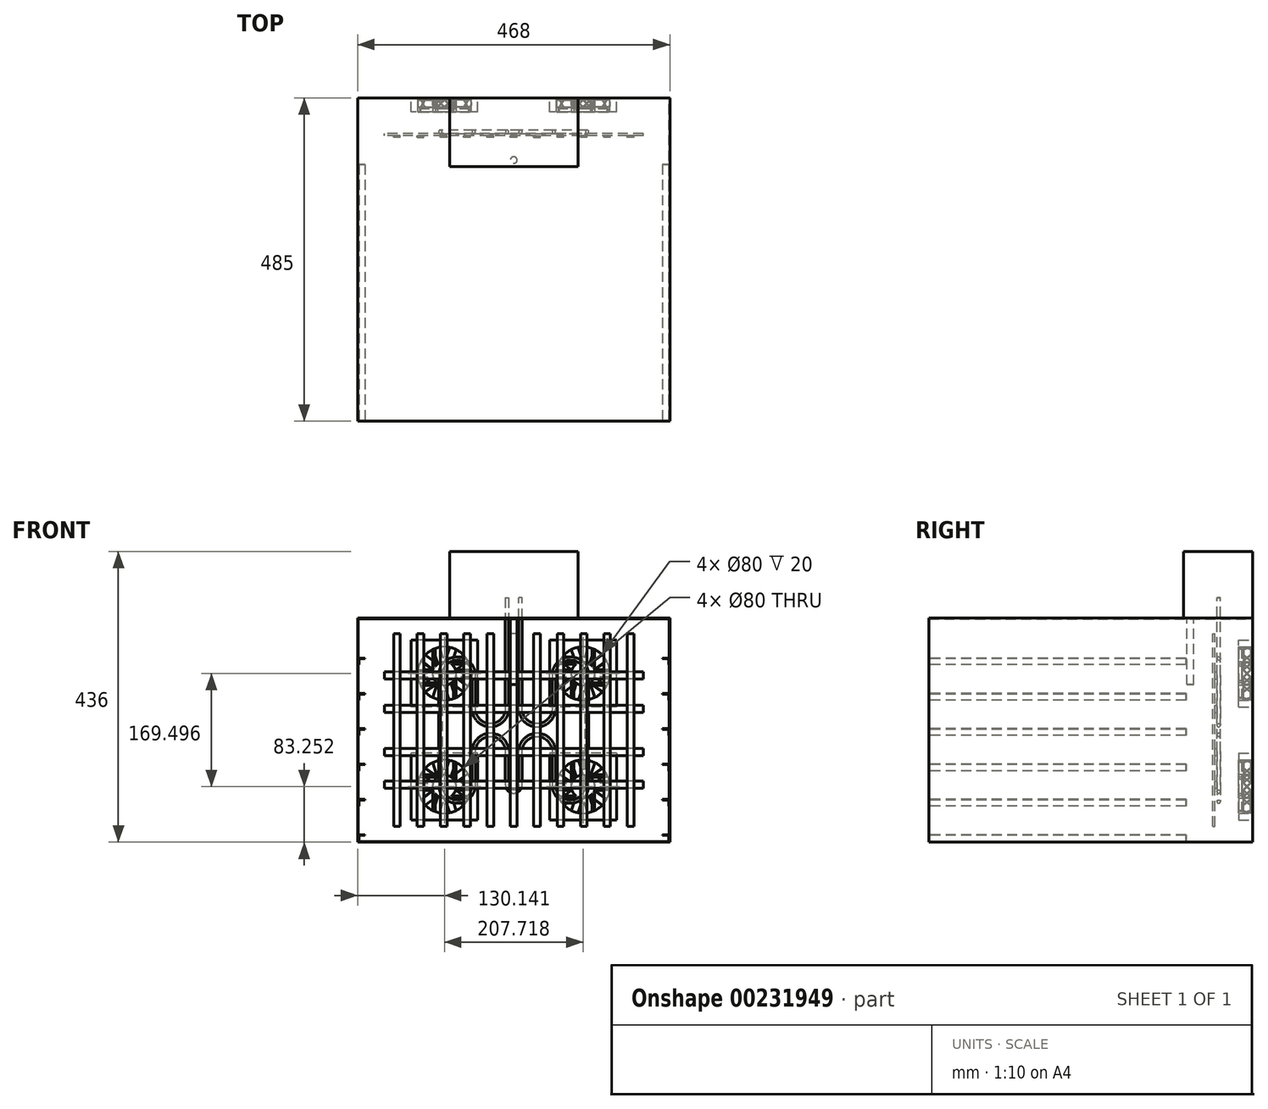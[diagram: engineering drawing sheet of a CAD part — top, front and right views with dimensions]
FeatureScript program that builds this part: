
annotation { "Feature Type Name" : "Feature", "Feature Type Description" : "" }
export const myFeature = defineFeature(function(context is Context, id is Id, definition is map)
    precondition{}
    {
        {
            var Q0;
            Q0=qCreatedBy(makeId("Front.planeOp"),FACE);
            var sketch = newSketch(context, id + "F0", { "sketchPlane" : qUnion([Q0])});
            skLineSegment(sketch, "E0.bottom", {"start": v(234, -168) * mm, "end": v(-234, -168) * mm});
            skLineSegment(sketch, "E0.top", {"start": v(234, 168) * mm, "end": v(-234, 168) * mm});
            skLineSegment(sketch, "E0.left", {"start": v(234, -168) * mm, "end": v(234, 168) * mm});
            skLineSegment(sketch, "E0.right", {"start": v(-234, -168) * mm, "end": v(-234, 168) * mm});
            skPoint(sketch, "E0.middle", {"position": v(0, 0) * mm});
            skSolve(sketch);
        }
        {
            var Q0;
            Q0 = qSketchRegion(id + "F0", true);
            extrude(context, id + "F1", {"entities" : qUnion([Q0]), "depth" : (385 + 50 + 50) * mm});
        }
        {
            var Q0;
            Q0=makeQuery(id+"F1.opExtrude","CAP_FACE",FACE,{"disambiguationData":[OSD([sQuery(id+"F0.wireOp",EDGE,"E0.bottom"),sQuery(id+"F0.wireOp",EDGE,"E0.top"),sQuery(id+"F0.wireOp",EDGE,"E0.left"),sQuery(id+"F0.wireOp",EDGE,"E0.right")])],"isStart":false});
            shell(context, id + "F2", {"entities" : qUnion([Q0]), "thickness" : 1 * mm});
        }
        {
            var Q0;
            Q0=makeQuery(id+"F1.opExtrude","CAP_FACE",FACE,{"disambiguationData":[OSD([sQuery(id+"F0.wireOp",EDGE,"E0.bottom"),sQuery(id+"F0.wireOp",EDGE,"E0.top"),sQuery(id+"F0.wireOp",EDGE,"E0.left"),sQuery(id+"F0.wireOp",EDGE,"E0.right")])],"isStart":false});
            var sketch = newSketch(context, id + "F3", { "sketchPlane" : qUnion([Q0])});
            skLineSegment(sketch, "E1", {"start": v(-233, -167) * mm, "end": v(-233, -157) * mm});
            skLineSegment(sketch, "E2", {"start": v(-233, -157) * mm, "end": v(-223, -157) * mm});
            skLineSegment(sketch, "E3", {"start": v(-223, -157) * mm, "end": v(-223, -158) * mm});
            skLineSegment(sketch, "E4", {"start": v(-223, -158) * mm, "end": v(-232, -158) * mm});
            skLineSegment(sketch, "E5", {"start": v(-232, -158) * mm, "end": v(-232, -167) * mm});
            skLineSegment(sketch, "E6", {"start": v(-232, -167) * mm, "end": v(-233, -167) * mm});
            skLineSegment(sketch, "E7.0.1.0", {"start": v(-232, -105) * mm, "end": v(-232, -114) * mm});
            skLineSegment(sketch, "E7.0.1.1", {"start": v(-223, -105) * mm, "end": v(-232, -105) * mm});
            skLineSegment(sketch, "E7.0.1.2", {"start": v(-233, -104) * mm, "end": v(-223, -104) * mm});
            skLineSegment(sketch, "E7.0.1.3", {"start": v(-233, -114) * mm, "end": v(-233, -104) * mm});
            skLineSegment(sketch, "E7.0.1.4", {"start": v(-232, -114) * mm, "end": v(-233, -114) * mm});
            skLineSegment(sketch, "E7.0.1.5", {"start": v(-223, -104) * mm, "end": v(-223, -105) * mm});
            skLineSegment(sketch, "E7.0.2.0", {"start": v(-232, -52) * mm, "end": v(-232, -61) * mm});
            skLineSegment(sketch, "E7.0.2.1", {"start": v(-223, -52) * mm, "end": v(-232, -52) * mm});
            skLineSegment(sketch, "E7.0.2.2", {"start": v(-233, -51) * mm, "end": v(-223, -51) * mm});
            skLineSegment(sketch, "E7.0.2.3", {"start": v(-233, -61) * mm, "end": v(-233, -51) * mm});
            skLineSegment(sketch, "E7.0.2.4", {"start": v(-232, -61) * mm, "end": v(-233, -61) * mm});
            skLineSegment(sketch, "E7.0.2.5", {"start": v(-223, -51) * mm, "end": v(-223, -52) * mm});
            skLineSegment(sketch, "E7.0.3.0", {"start": v(-232, 1) * mm, "end": v(-232, -8) * mm});
            skLineSegment(sketch, "E7.0.3.1", {"start": v(-223, 1) * mm, "end": v(-232, 1) * mm});
            skLineSegment(sketch, "E7.0.3.2", {"start": v(-233, 2) * mm, "end": v(-223, 2) * mm});
            skLineSegment(sketch, "E7.0.3.3", {"start": v(-233, -8) * mm, "end": v(-233, 2) * mm});
            skLineSegment(sketch, "E7.0.3.4", {"start": v(-232, -8) * mm, "end": v(-233, -8) * mm});
            skLineSegment(sketch, "E7.0.3.5", {"start": v(-223, 2) * mm, "end": v(-223, 1) * mm});
            skLineSegment(sketch, "E7.0.4.0", {"start": v(-232, 54) * mm, "end": v(-232, 45) * mm});
            skLineSegment(sketch, "E7.0.4.1", {"start": v(-223, 54) * mm, "end": v(-232, 54) * mm});
            skLineSegment(sketch, "E7.0.4.2", {"start": v(-233, 55) * mm, "end": v(-223, 55) * mm});
            skLineSegment(sketch, "E7.0.4.3", {"start": v(-233, 45) * mm, "end": v(-233, 55) * mm});
            skLineSegment(sketch, "E7.0.4.4", {"start": v(-232, 45) * mm, "end": v(-233, 45) * mm});
            skLineSegment(sketch, "E7.0.4.5", {"start": v(-223, 55) * mm, "end": v(-223, 54) * mm});
            skLineSegment(sketch, "E7.0.5.0", {"start": v(-232, 107) * mm, "end": v(-232, 98) * mm});
            skLineSegment(sketch, "E7.0.5.1", {"start": v(-223, 107) * mm, "end": v(-232, 107) * mm});
            skLineSegment(sketch, "E7.0.5.2", {"start": v(-233, 108) * mm, "end": v(-223, 108) * mm});
            skLineSegment(sketch, "E7.0.5.3", {"start": v(-233, 98) * mm, "end": v(-233, 108) * mm});
            skLineSegment(sketch, "E7.0.5.4", {"start": v(-232, 98) * mm, "end": v(-233, 98) * mm});
            skLineSegment(sketch, "E7.0.5.5", {"start": v(-223, 108) * mm, "end": v(-223, 107) * mm});
            skLineSegment(sketch, "E7.direction1", {"start": v(-233, -167) * mm, "end": v(-208, -167) * mm, "construction": true});
            skLineSegment(sketch, "E7.direction2", {"start": v(-233, -167) * mm, "end": v(-233, -114) * mm, "construction": true});
            skSolve(sketch);
        }
        {
            var Q0;
            Q0 = qSketchRegion(id + "F3", true);
            var Q1;
            Q1 = qConstructionFilter(qBodyType(qCreatedBy(id + "F3" ,EDGE), BodyType.WIRE), ConstructionObject.NO);
            extrude(context, id + "F4", {"entities" : qUnion([Q0]), "surfaceEntities" : qUnion([Q1]), "oppositeDirection" : true, "depth" : 385 * mm});
        }
        {
            var Q0;
            Q0=makeQuery(id+"F4.opExtrude","SWEPT_BODY",BODY,{"disambiguationData":[OSD([sQuery(id+"F3.wireOp",EDGE,"E7.0.5.0"),sQuery(id+"F3.wireOp",EDGE,"E7.0.5.1"),sQuery(id+"F3.wireOp",EDGE,"E7.0.5.2"),sQuery(id+"F3.wireOp",EDGE,"E7.0.5.3"),sQuery(id+"F3.wireOp",EDGE,"E7.0.5.4"),sQuery(id+"F3.wireOp",EDGE,"E7.0.5.5")])]});
            var Q1;
            Q1=makeQuery(id+"F4.opExtrude","SWEPT_BODY",BODY,{"disambiguationData":[OSD([sQuery(id+"F3.wireOp",EDGE,"E7.0.4.0"),sQuery(id+"F3.wireOp",EDGE,"E7.0.4.1"),sQuery(id+"F3.wireOp",EDGE,"E7.0.4.2"),sQuery(id+"F3.wireOp",EDGE,"E7.0.4.3"),sQuery(id+"F3.wireOp",EDGE,"E7.0.4.4"),sQuery(id+"F3.wireOp",EDGE,"E7.0.4.5")])]});
            var Q2;
            Q2=makeQuery(id+"F4.opExtrude","SWEPT_BODY",BODY,{"disambiguationData":[OSD([sQuery(id+"F3.wireOp",EDGE,"E7.0.3.0"),sQuery(id+"F3.wireOp",EDGE,"E7.0.3.1"),sQuery(id+"F3.wireOp",EDGE,"E7.0.3.2"),sQuery(id+"F3.wireOp",EDGE,"E7.0.3.3"),sQuery(id+"F3.wireOp",EDGE,"E7.0.3.4"),sQuery(id+"F3.wireOp",EDGE,"E7.0.3.5")])]});
            var Q3;
            Q3=makeQuery(id+"F4.opExtrude","SWEPT_BODY",BODY,{"disambiguationData":[OSD([sQuery(id+"F3.wireOp",EDGE,"E7.0.2.0"),sQuery(id+"F3.wireOp",EDGE,"E7.0.2.1"),sQuery(id+"F3.wireOp",EDGE,"E7.0.2.2"),sQuery(id+"F3.wireOp",EDGE,"E7.0.2.3"),sQuery(id+"F3.wireOp",EDGE,"E7.0.2.4"),sQuery(id+"F3.wireOp",EDGE,"E7.0.2.5")])]});
            var Q4;
            Q4=makeQuery(id+"F4.opExtrude","SWEPT_BODY",BODY,{"disambiguationData":[OSD([sQuery(id+"F3.wireOp",EDGE,"E7.0.1.0"),sQuery(id+"F3.wireOp",EDGE,"E7.0.1.1"),sQuery(id+"F3.wireOp",EDGE,"E7.0.1.2"),sQuery(id+"F3.wireOp",EDGE,"E7.0.1.3"),sQuery(id+"F3.wireOp",EDGE,"E7.0.1.4"),sQuery(id+"F3.wireOp",EDGE,"E7.0.1.5")])]});
            var Q5;
            Q5=makeQuery(id+"F4.opExtrude","SWEPT_BODY",BODY,{"disambiguationData":[OSD([sQuery(id+"F3.wireOp",EDGE,"E1"),sQuery(id+"F3.wireOp",EDGE,"E2"),sQuery(id+"F3.wireOp",EDGE,"E3"),sQuery(id+"F3.wireOp",EDGE,"E4"),sQuery(id+"F3.wireOp",EDGE,"E5"),sQuery(id+"F3.wireOp",EDGE,"E6")])]});
            var Q6;
            Q6=qCreatedBy(makeId("Right.planeOp"),FACE);
            mirror(context, id + "F5", {"entities" : qUnion([Q0, Q1, Q2, Q3, Q4, Q5]), "mirrorPlane" : qUnion([Q6])});
        }
        {
            var Q0;
            Q0=makeQuery(id+"F1.opExtrude","CAP_FACE",FACE,{"disambiguationData":[OSD([sQuery(id+"F0.wireOp",EDGE,"E0.bottom"),sQuery(id+"F0.wireOp",EDGE,"E0.top"),sQuery(id+"F0.wireOp",EDGE,"E0.left"),sQuery(id+"F0.wireOp",EDGE,"E0.right")])],"isStart":true});
            var sketch = newSketch(context, id + "F6", { "sketchPlane" : qUnion([Q0])});
            skCircle(sketch, "E8", {"center": v(-103.86, 84.75) * mm, "radius": 40 * mm});
            skCircle(sketch, "E9", {"center": v(103.86, 84.75) * mm, "radius": 40 * mm});
            skCircle(sketch, "E10", {"center": v(103.86, -84.75) * mm, "radius": 40 * mm});
            skCircle(sketch, "E11", {"center": v(-103.86, -84.75) * mm, "radius": 40 * mm});
            skLineSegment(sketch, "E12", {"start": v(0, 0) * mm, "end": v(0, 0) * mm});
            skPoint(sketch, "E12.endSnap0", {"position": v(0, -168) * mm});
            skLineSegment(sketch, "E13", {"start": v(0, 0) * mm, "end": v(275.26, 0) * mm, "construction": true});
            skLineSegment(sketch, "E14", {"start": v(-103.86, 84.75) * mm, "end": v(103.86, 84.75) * mm, "construction": true});
            skLineSegment(sketch, "E15", {"start": v(103.86, 84.75) * mm, "end": v(103.86, -84.75) * mm, "construction": true});
            skLineSegment(sketch, "E16", {"start": v(-103.86, -84.75) * mm, "end": v(-103.86, 84.75) * mm, "construction": true});
            skLineSegment(sketch, "E17", {"start": v(103.86, -84.75) * mm, "end": v(-103.86, -84.75) * mm, "construction": true});
            skSolve(sketch);
        }
        {
            var Q0;
            Q0 = qSketchRegion(id + "F6", true);
            extrude(context, id + "F7", {"entities" : qUnion([Q0]), "operationType" : NewBodyOperationType.REMOVE, "endBound" : BoundingType.THROUGH_ALL, "oppositeDirection" : true, "depth" : 25 * mm});
        }
        {
            var Q0;
            Q0=makeQuery(id+"F2.opShell","OFFSET_FACE",FACE,{"disambiguationData":[OSD([sQuery(id+"F0.wireOp",EDGE,"E0.bottom"),sQuery(id+"F0.wireOp",EDGE,"E0.top"),sQuery(id+"F0.wireOp",EDGE,"E0.left"),sQuery(id+"F0.wireOp",EDGE,"E0.right")])]});
            var sketch = newSketch(context, id + "F8", { "sketchPlane" : qUnion([Q0])});
            skCircle(sketch, "E18.0", {"center": v(-103.86, 84.75) * mm, "radius": 40 * mm});
            skCircle(sketch, "E19.0", {"center": v(103.86, 84.75) * mm, "radius": 40 * mm});
            skCircle(sketch, "E20.0", {"center": v(103.86, -84.75) * mm, "radius": 40 * mm});
            skCircle(sketch, "E21.0", {"center": v(-103.86, -84.75) * mm, "radius": 40 * mm});
            skLineSegment(sketch, "E22.bottom", {"start": v(-53.86, 34.75) * mm, "end": v(-153.86, 34.75) * mm});
            skLineSegment(sketch, "E22.top", {"start": v(-53.86, 134.75) * mm, "end": v(-153.86, 134.75) * mm});
            skLineSegment(sketch, "E22.left", {"start": v(-53.86, 34.75) * mm, "end": v(-53.86, 134.75) * mm});
            skLineSegment(sketch, "E22.right", {"start": v(-153.86, 34.75) * mm, "end": v(-153.86, 134.75) * mm});
            skLineSegment(sketch, "E23.bottom", {"start": v(153.86, 34.75) * mm, "end": v(53.86, 34.75) * mm});
            skLineSegment(sketch, "E23.top", {"start": v(153.86, 134.75) * mm, "end": v(53.86, 134.75) * mm});
            skLineSegment(sketch, "E23.left", {"start": v(153.86, 34.75) * mm, "end": v(153.86, 134.75) * mm});
            skLineSegment(sketch, "E23.right", {"start": v(53.86, 34.75) * mm, "end": v(53.86, 134.75) * mm});
            skLineSegment(sketch, "E24.bottom", {"start": v(153.86, -34.75) * mm, "end": v(53.86, -34.75) * mm});
            skLineSegment(sketch, "E24.top", {"start": v(153.86, -134.75) * mm, "end": v(53.86, -134.75) * mm});
            skLineSegment(sketch, "E24.left", {"start": v(153.86, -34.75) * mm, "end": v(153.86, -134.75) * mm});
            skLineSegment(sketch, "E24.right", {"start": v(53.86, -34.75) * mm, "end": v(53.86, -134.75) * mm});
            skLineSegment(sketch, "E25.bottom", {"start": v(-53.86, -134.75) * mm, "end": v(-153.86, -134.75) * mm});
            skLineSegment(sketch, "E25.top", {"start": v(-53.86, -34.75) * mm, "end": v(-153.86, -34.75) * mm});
            skLineSegment(sketch, "E25.left", {"start": v(-53.86, -134.75) * mm, "end": v(-53.86, -34.75) * mm});
            skLineSegment(sketch, "E25.right", {"start": v(-153.86, -134.75) * mm, "end": v(-153.86, -34.75) * mm});
            skSolve(sketch);
        }
        {
            var Q0;
            Q0 = qSketchRegion(id + "F8", true);
            extrude(context, id + "F9", {"entities" : qUnion([Q0]), "depth" : 20 * mm});
        }
        {
            var Q0;
            Q0=makeQuery(id+"F2.opShell","OFFSET_FACE",FACE,{"disambiguationData":[OSD([sQuery(id+"F0.wireOp",EDGE,"E0.bottom"),sQuery(id+"F0.wireOp",EDGE,"E0.top"),sQuery(id+"F0.wireOp",EDGE,"E0.left"),sQuery(id+"F0.wireOp",EDGE,"E0.right")])]});
            cPlane(context, id + "F10", {"entities" : qUnion([Q0]), "cplaneType" : CPlaneType.OFFSET, "offset" : 50 * mm, "width" : 150 * mm, "height" : 150 * mm});
        }
        {
            var Q0;
            Q0=qCreatedBy(id+"F10.planeOp",FACE);
            var sketch = newSketch(context, id + "F11", { "sketchPlane" : qUnion([Q0])});
            skLineSegment(sketch, "E26", {"start": v(-10, 198.33) * mm, "end": v(-10, 32.24) * mm});
            skLineSegment(sketch, "E27", {"start": v(10, 198.33) * mm, "end": v(10, 32.24) * mm});
            skLineSegment(sketch, "E28", {"start": v(-60, 32.24) * mm, "end": v(-60, 82.24) * mm});
            skLineSegment(sketch, "E29", {"start": v(-110, 82.24) * mm, "end": v(-110, -82.24) * mm});
            skLineSegment(sketch, "E30", {"start": v(-60, -82.24) * mm, "end": v(-60, -32.24) * mm});
            skLineSegment(sketch, "E31", {"start": v(-10, -32.24) * mm, "end": v(-10, -82.24) * mm});
            skLineSegment(sketch, "E32", {"start": v(10, -82.24) * mm, "end": v(10, -32.24) * mm});
            skLineSegment(sketch, "E33", {"start": v(60, -32.24) * mm, "end": v(60, -82.24) * mm});
            skLineSegment(sketch, "E34", {"start": v(110, -82.24) * mm, "end": v(110, 82.24) * mm});
            skLineSegment(sketch, "E35", {"start": v(60, 82.24) * mm, "end": v(60, 32.24) * mm});
            skLineSegment(sketch, "E36", {"start": v(0, 0) * mm, "end": v(0, 56.52) * mm, "construction": true});
            skArc(sketch, "E37", {"start": v(-60, 32.24) * mm, "mid": v(-35, 7.24) * mm, "end": v(-10, 32.24) * mm});
            skArc(sketch, "E38", {"start": v(-60, 82.24) * mm, "mid": v(-85, 107.24) * mm, "end": v(-110, 82.24) * mm});
            skArc(sketch, "E39", {"start": v(10, 32.24) * mm, "mid": v(35, 7.24) * mm, "end": v(60, 32.24) * mm});
            skArc(sketch, "E40", {"start": v(110, 82.24) * mm, "mid": v(85, 107.24) * mm, "end": v(60, 82.24) * mm});
            skArc(sketch, "E41", {"start": v(60, -82.24) * mm, "mid": v(85, -107.24) * mm, "end": v(110, -82.24) * mm});
            skArc(sketch, "E42", {"start": v(60, -32.24) * mm, "mid": v(35, -7.24) * mm, "end": v(10, -32.24) * mm});
            skArc(sketch, "E43", {"start": v(-10, -82.24) * mm, "mid": v(0, -92.24) * mm, "end": v(10, -82.24) * mm});
            skArc(sketch, "E44", {"start": v(-10, -32.24) * mm, "mid": v(-35, -7.24) * mm, "end": v(-60, -32.24) * mm});
            skArc(sketch, "E45", {"start": v(-110, -82.24) * mm, "mid": v(-85, -107.24) * mm, "end": v(-60, -82.24) * mm});
            skLineSegment(sketch, "E46", {"start": v(-60, -32.24) * mm, "end": v(60, -32.24) * mm, "construction": true});
            skLineSegment(sketch, "E47", {"start": v(-60, 32.24) * mm, "end": v(60, 32.24) * mm, "construction": true});
            skLineSegment(sketch, "E48", {"start": v(0, 0) * mm, "end": v(72.76, 0) * mm, "construction": true});
            skSolve(sketch);
        }
        {
            var Q0;
            Q0=sQuery(id+"F11.wireOp",EDGE,"E26");
            var Q1;
            Q1=sQuery(id+"F11.wireOp",VERTEX,"E26.start");
            cPlane(context, id + "F12", {"entities" : qUnion([Q0, Q1]), "cplaneType" : CPlaneType.LINE_POINT, "offset" : 25 * mm, "width" : 150 * mm, "height" : 150 * mm});
        }
        {
            var Q0;
            Q0=qCreatedBy(id+"F12.planeOp",FACE);
            var sketch = newSketch(context, id + "F13", { "sketchPlane" : qUnion([Q0])});
            skCircle(sketch, "E49", {"center": v(-10, 51) * mm, "radius": 2.5 * mm});
            skSolve(sketch);
        }
        {
            var Q0;
            Q0=makeQuery(id+"F13.imprint","IMPRINT",FACE,{"disambiguationData":[TD([[makeQuery(id+"F13.imprint","IMPRINT",EDGE,{"derivedFrom":sQuery(id+"F13.wireOp",EDGE,"E49")}),1.0]])]});
            var Q1;
            Q1 = qConstructionFilter(qBodyType(qCreatedBy(id + "F11" ,EDGE), BodyType.WIRE), ConstructionObject.NO);
            sweep(context, id + "F14", {"profiles" : qUnion([Q0]), "path" : qUnion([Q1])});
        }
        {
            var Q0;
            Q0=qCreatedBy(id+"F10.planeOp",FACE);
            cPlane(context, id + "F15", {"entities" : qUnion([Q0]), "cplaneType" : CPlaneType.OFFSET, "offset" : 2.5 * mm, "width" : 150 * mm, "height" : 150 * mm});
        }
        {
            var Q0;
            Q0=qCreatedBy(id+"F15.planeOp",FACE);
            var sketch = newSketch(context, id + "F16", { "sketchPlane" : qUnion([Q0])});
            skLineSegment(sketch, "E50.bottom", {"start": v(193.88, 26.5) * mm, "end": v(-193.88, 26.5) * mm});
            skLineSegment(sketch, "E50.top", {"start": v(193.88, 37.1) * mm, "end": v(-193.88, 37.1) * mm});
            skLineSegment(sketch, "E50.left", {"start": v(193.88, 26.5) * mm, "end": v(193.88, 37.1) * mm});
            skLineSegment(sketch, "E50.right", {"start": v(-193.88, 26.5) * mm, "end": v(-193.88, 37.1) * mm});
            skPoint(sketch, "E50.middle", {"position": v(0, 31.8) * mm});
            skLineSegment(sketch, "E51.bottom", {"start": v(193.88, 76.52) * mm, "end": v(-193.88, 76.52) * mm});
            skLineSegment(sketch, "E51.top", {"start": v(193.88, 87.12) * mm, "end": v(-193.88, 87.12) * mm});
            skLineSegment(sketch, "E51.left", {"start": v(193.88, 76.52) * mm, "end": v(193.88, 87.12) * mm});
            skLineSegment(sketch, "E51.right", {"start": v(-193.88, 76.52) * mm, "end": v(-193.88, 87.12) * mm});
            skPoint(sketch, "E51.middle", {"position": v(0, 81.82) * mm});
            skLineSegment(sketch, "E52.bottom", {"start": v(193.88, -38.07) * mm, "end": v(-193.88, -38.07) * mm});
            skLineSegment(sketch, "E52.top", {"start": v(193.88, -27.47) * mm, "end": v(-193.88, -27.47) * mm});
            skLineSegment(sketch, "E52.left", {"start": v(193.88, -38.07) * mm, "end": v(193.88, -27.47) * mm});
            skLineSegment(sketch, "E52.right", {"start": v(-193.88, -38.07) * mm, "end": v(-193.88, -27.47) * mm});
            skPoint(sketch, "E52.middle", {"position": v(0, -32.77) * mm});
            skLineSegment(sketch, "E53.bottom", {"start": v(193.88, -87.18) * mm, "end": v(-193.88, -87.18) * mm});
            skLineSegment(sketch, "E53.top", {"start": v(193.88, -76.58) * mm, "end": v(-193.88, -76.58) * mm});
            skLineSegment(sketch, "E53.left", {"start": v(193.88, -87.18) * mm, "end": v(193.88, -76.58) * mm});
            skLineSegment(sketch, "E53.right", {"start": v(-193.88, -87.18) * mm, "end": v(-193.88, -76.58) * mm});
            skPoint(sketch, "E53.middle", {"position": v(0, -81.88) * mm});
            skSolve(sketch);
        }
        {
            var Q0;
            Q0 = qSketchRegion(id + "F16", true);
            extrude(context, id + "F17", {"entities" : qUnion([Q0]), "operationType" : NewBodyOperationType.ADD, "depth" : 3 * mm});
        }
        {
            var Q0;
            Q0=makeQuery(id+"F1.opExtrude","SWEPT_FACE",FACE,{"disambiguationData":[OSD([sQuery(id+"F0.wireOp",EDGE,"E0.top")])]});
            var sketch = newSketch(context, id + "F18", { "sketchPlane" : qUnion([Q0])});
            skLineSegment(sketch, "E54.bottom", {"start": v(96.2, 0) * mm, "end": v(-96.2, 0) * mm});
            skLineSegment(sketch, "E54.top", {"start": v(96.2, -103.28) * mm, "end": v(-96.2, -103.28) * mm});
            skLineSegment(sketch, "E54.left", {"start": v(96.2, 0) * mm, "end": v(96.2, -103.28) * mm});
            skLineSegment(sketch, "E54.right", {"start": v(-96.2, 0) * mm, "end": v(-96.2, -103.28) * mm});
            skPoint(sketch, "E54.middle", {"position": v(0, -51.64) * mm});
            skSolve(sketch);
        }
        {
            var Q0;
            Q0 = qSketchRegion(id + "F18", true);
            extrude(context, id + "F19", {"entities" : qUnion([Q0]), "depth" : 100 * mm});
        }
        {
            var Q0;
            Q0=makeQuery(id+"F1.opExtrude","SWEPT_FACE",FACE,{"disambiguationData":[OSD([sQuery(id+"F0.wireOp",EDGE,"E0.top")])]});
            var sketch = newSketch(context, id + "F20", { "sketchPlane" : qUnion([Q0])});
            skCircle(sketch, "E55", {"center": v(0, -93.28) * mm, "radius": 5 * mm});
            skSolve(sketch);
        }
        {
            var Q0;
            Q0 = qSketchRegion(id + "F20", true);
            extrude(context, id + "F21", {"entities" : qUnion([Q0]), "oppositeDirection" : true, "depth" : 100 * mm});
        }
        {
            var Q0;
            Q0=makeQuery(id+"F9.opExtrude","CAP_FACE",FACE,{"disambiguationData":[OSD([sQuery(id+"F8.wireOp",EDGE,"E18.0"),sQuery(id+"F8.wireOp",EDGE,"E22.bottom"),sQuery(id+"F8.wireOp",EDGE,"E22.top"),sQuery(id+"F8.wireOp",EDGE,"E22.left"),sQuery(id+"F8.wireOp",EDGE,"E22.right")])],"isStart":false});
            var sketch = newSketch(context, id + "F22", { "sketchPlane" : qUnion([Q0])});
            skCircle(sketch, "E56.0", {"center": v(-103.86, 84.75) * mm, "radius": 40 * mm, "construction": true});
            skCircle(sketch, "E57", {"center": v(-103.86, 84.75) * mm, "radius": 17.5 * mm});
            skSolve(sketch);
        }
        {
            var Q0;
            Q0 = qSketchRegion(id + "F22", true);
            extrude(context, id + "F23", {"entities" : qUnion([Q0]), "oppositeDirection" : true, "depth" : 20 * mm});
        }
        {
            var Q0;
            Q0=makeQuery(id+"F9.opExtrude","CAP_FACE",FACE,{"disambiguationData":[OSD([sQuery(id+"F8.wireOp",EDGE,"E18.0"),sQuery(id+"F8.wireOp",EDGE,"E22.bottom"),sQuery(id+"F8.wireOp",EDGE,"E22.top"),sQuery(id+"F8.wireOp",EDGE,"E22.left"),sQuery(id+"F8.wireOp",EDGE,"E22.right")])],"isStart":false});
            var sketch = newSketch(context, id + "F24", { "sketchPlane" : qUnion([Q0])});
            skCircle(sketch, "E58.0", {"center": v(-103.86, 84.75) * mm, "radius": 17.5 * mm, "construction": true});
            skCircle(sketch, "E59.0", {"center": v(-103.86, 84.75) * mm, "radius": 40 * mm, "construction": true});
            skLineSegment(sketch, "E60", {"start": v(-103.86, 67.25) * mm, "end": v(-139.83, 67.25) * mm});
            skLineSegment(sketch, "E61", {"start": v(-139.83, 67.25) * mm, "end": v(-141.42, 70.99) * mm});
            skLineSegment(sketch, "E62", {"start": v(-141.42, 70.99) * mm, "end": v(-114.67, 70.99) * mm});
            skLineSegment(sketch, "E63", {"start": v(-114.67, 70.99) * mm, "end": v(-103.86, 67.25) * mm});
            skLineSegment(sketch, "E64", {"start": v(-141.42, 70.99) * mm, "end": v(-139.83, 67.25) * mm});
            skLineSegment(sketch, "E65.1.0", {"start": v(-86.36, 84.75) * mm, "end": v(-86.36, 48.78) * mm});
            skLineSegment(sketch, "E65.1.1", {"start": v(-90.1, 47.19) * mm, "end": v(-90.1, 73.94) * mm});
            skLineSegment(sketch, "E65.1.2", {"start": v(-90.1, 73.94) * mm, "end": v(-86.36, 84.75) * mm});
            skLineSegment(sketch, "E65.1.3", {"start": v(-90.1, 47.19) * mm, "end": v(-86.36, 48.78) * mm});
            skLineSegment(sketch, "E65.1.4", {"start": v(-86.36, 48.78) * mm, "end": v(-90.1, 47.19) * mm});
            skLineSegment(sketch, "E65.2.0", {"start": v(-103.86, 102.25) * mm, "end": v(-67.9, 102.25) * mm});
            skLineSegment(sketch, "E65.2.1", {"start": v(-66.3, 98.5) * mm, "end": v(-93.05, 98.5) * mm});
            skLineSegment(sketch, "E65.2.2", {"start": v(-93.05, 98.5) * mm, "end": v(-103.86, 102.25) * mm});
            skLineSegment(sketch, "E65.2.3", {"start": v(-66.3, 98.5) * mm, "end": v(-67.9, 102.25) * mm});
            skLineSegment(sketch, "E65.2.4", {"start": v(-67.9, 102.25) * mm, "end": v(-66.3, 98.5) * mm});
            skLineSegment(sketch, "E65.3.0", {"start": v(-121.36, 84.75) * mm, "end": v(-121.36, 120.72) * mm});
            skLineSegment(sketch, "E65.3.1", {"start": v(-117.62, 122.3) * mm, "end": v(-117.62, 95.56) * mm});
            skLineSegment(sketch, "E65.3.2", {"start": v(-117.62, 95.56) * mm, "end": v(-121.36, 84.75) * mm});
            skLineSegment(sketch, "E65.3.3", {"start": v(-117.62, 122.3) * mm, "end": v(-121.36, 120.72) * mm});
            skLineSegment(sketch, "E65.3.4", {"start": v(-121.36, 120.72) * mm, "end": v(-117.62, 122.3) * mm});
            skSolve(sketch);
        }
        {
            var Q0;
            Q0 = qSketchRegion(id + "F24", true);
            extrude(context, id + "F25", {"entities" : qUnion([Q0]), "operationType" : NewBodyOperationType.ADD, "oppositeDirection" : true, "depth" : 5 * mm});
        }
        {
            var Q0;
            Q0=makeQuery(id+"F25.opExtrude","SWEPT_FACE",FACE,{"disambiguationData":[OSD([sQuery(id+"F24.wireOp",EDGE,"E65.1.0")])]});
            var sketch = newSketch(context, id + "F26", { "sketchPlane" : qUnion([Q0])});
            skLineSegment(sketch, "E66", {"start": v(-13.45, 90.4) * mm, "end": v(-2.84, 79.8) * mm});
            skLineSegment(sketch, "E67", {"start": v(-2.84, 79.8) * mm, "end": v(-3.55, 79.1) * mm});
            skLineSegment(sketch, "E68", {"start": v(-3.55, 79.1) * mm, "end": v(-14.16, 89.7) * mm});
            skLineSegment(sketch, "E69", {"start": v(-14.16, 89.7) * mm, "end": v(-13.45, 90.4) * mm});
            skLineSegment(sketch, "E70.0", {"start": v(-1, 67.25) * mm, "end": v(-1, 102.25) * mm, "construction": true});
            skLineSegment(sketch, "E71", {"start": v(-1, 84.75) * mm, "end": v(-25.24, 84.75) * mm, "construction": true});
            skLineSegment(sketch, "E72.0", {"start": v(-16, 84.75) * mm, "end": v(-16, 48.78) * mm, "construction": true});
            skLineSegment(sketch, "E73", {"start": v(-8.5, 96.57) * mm, "end": v(-8.5, 73.04) * mm, "construction": true});
            skLineSegment(sketch, "E74", {"start": v(-18.17, 94.41) * mm, "end": v(0, 76.25) * mm, "construction": true});
            skLineSegment(sketch, "E75", {"start": v(-3.28, 89.96) * mm, "end": v(-8.44, 84.81) * mm, "construction": true});
            skPoint(sketch, "E76", {"position": v(-8.5, 84.75) * mm});
            skSolve(sketch);
        }
        {
            var Q0;
            Q0 = qSketchRegion(id + "F26", true);
            var Q1;
            Q1=makeQuery(id+"F9.opExtrude","SWEPT_FACE",FACE,{"disambiguationData":[OSD([sQuery(id+"F8.wireOp",EDGE,"E18.0")])]});
            var Q2;
            Q2=makeQuery(id+"F23.opExtrude","SWEPT_FACE",FACE,{"disambiguationData":[OSD([sQuery(id+"F22.wireOp",EDGE,"E57")])]});
            extrude(context, id + "F27", {"entities" : qUnion([Q0]), "endBound" : BoundingType.UP_TO_SURFACE, "endBoundEntityFace" : qUnion([Q1]), "depth" : 25 * mm, "hasSecondDirection" : true, "secondDirectionBound" : SecondDirectionBoundingType.UP_TO_SURFACE, "secondDirectionOppositeDirection" : true, "secondDirectionBoundEntityFace" : qUnion([Q2]), "secondDirectionDepth" : 25 * mm});
        }
        {
            var Q0;
            Q0=makeQuery(id+"F27.opExtrude","SWEPT_BODY",BODY,{"disambiguationData":[OSD([sQuery(id+"F26.wireOp",EDGE,"E66"),sQuery(id+"F26.wireOp",EDGE,"E67"),sQuery(id+"F26.wireOp",EDGE,"E68"),sQuery(id+"F26.wireOp",EDGE,"E69")])]});
            var Q1;
            Q1=makeQuery(id+"F23.opExtrude","SWEPT_FACE",FACE,{"disambiguationData":[OSD([sQuery(id+"F22.wireOp",EDGE,"E57")])]});
            circularPattern(context, id + "F28", {"entities" : qUnion([Q0]), "axis" : qUnion([Q1]), "angle" : 360 * degree, "instanceCount" : 10, "equalSpace" : true});
        }
        {
            var Q0;
            Q0=makeQuery(id+"F28.opPattern","COPY",BODY,{"derivedFrom":makeQuery(id+"F27.opExtrude","SWEPT_BODY",BODY,{"disambiguationData":[OSD([sQuery(id+"F26.wireOp",EDGE,"E66"),sQuery(id+"F26.wireOp",EDGE,"E67"),sQuery(id+"F26.wireOp",EDGE,"E68"),sQuery(id+"F26.wireOp",EDGE,"E69")])]}),"instanceName":"2"});
            var Q1;
            Q1=makeQuery(id+"F28.opPattern","COPY",BODY,{"derivedFrom":makeQuery(id+"F27.opExtrude","SWEPT_BODY",BODY,{"disambiguationData":[OSD([sQuery(id+"F26.wireOp",EDGE,"E66"),sQuery(id+"F26.wireOp",EDGE,"E67"),sQuery(id+"F26.wireOp",EDGE,"E68"),sQuery(id+"F26.wireOp",EDGE,"E69")])]}),"instanceName":"5"});
            var Q2;
            Q2=makeQuery(id+"F25.boolean.opBoolean","MERGE",BODY,{"derivedFrom":[makeQuery(id+"F9.opExtrude","SWEPT_BODY",BODY,{"disambiguationData":[OSD([sQuery(id+"F8.wireOp",EDGE,"E18.0"),sQuery(id+"F8.wireOp",EDGE,"E22.bottom"),sQuery(id+"F8.wireOp",EDGE,"E22.top"),sQuery(id+"F8.wireOp",EDGE,"E22.left"),sQuery(id+"F8.wireOp",EDGE,"E22.right")])]}),makeQuery(id+"F23.opExtrude","SWEPT_BODY",BODY,{"disambiguationData":[OSD([sQuery(id+"F22.wireOp",EDGE,"E57")])]}),makeQuery(id+"F25.opExtrude","SWEPT_BODY",BODY,{"disambiguationData":[OSD([sQuery(id+"F24.wireOp",EDGE,"E60"),sQuery(id+"F24.wireOp",EDGE,"E62"),sQuery(id+"F24.wireOp",EDGE,"E63"),sQuery(id+"F24.wireOp",EDGE,"E64")])]}),makeQuery(id+"F25.opExtrude","SWEPT_BODY",BODY,{"disambiguationData":[OSD([sQuery(id+"F24.wireOp",EDGE,"E65.1.0"),sQuery(id+"F24.wireOp",EDGE,"E65.1.1"),sQuery(id+"F24.wireOp",EDGE,"E65.1.2"),sQuery(id+"F24.wireOp",EDGE,"E65.1.4")])]}),makeQuery(id+"F25.opExtrude","SWEPT_BODY",BODY,{"disambiguationData":[OSD([sQuery(id+"F24.wireOp",EDGE,"E65.2.0"),sQuery(id+"F24.wireOp",EDGE,"E65.2.1"),sQuery(id+"F24.wireOp",EDGE,"E65.2.2"),sQuery(id+"F24.wireOp",EDGE,"E65.2.4")])]}),makeQuery(id+"F25.opExtrude","SWEPT_BODY",BODY,{"disambiguationData":[OSD([sQuery(id+"F24.wireOp",EDGE,"E65.3.0"),sQuery(id+"F24.wireOp",EDGE,"E65.3.1"),sQuery(id+"F24.wireOp",EDGE,"E65.3.2"),sQuery(id+"F24.wireOp",EDGE,"E65.3.4")])]})]});
            var Q3;
            Q3=makeQuery(id+"F28.opPattern","COPY",BODY,{"derivedFrom":makeQuery(id+"F27.opExtrude","SWEPT_BODY",BODY,{"disambiguationData":[OSD([sQuery(id+"F26.wireOp",EDGE,"E66"),sQuery(id+"F26.wireOp",EDGE,"E67"),sQuery(id+"F26.wireOp",EDGE,"E68"),sQuery(id+"F26.wireOp",EDGE,"E69")])]}),"instanceName":"8"});
            var Q4;
            Q4=makeQuery(id+"F27.opExtrude","SWEPT_BODY",BODY,{"disambiguationData":[OSD([sQuery(id+"F26.wireOp",EDGE,"E66"),sQuery(id+"F26.wireOp",EDGE,"E67"),sQuery(id+"F26.wireOp",EDGE,"E68"),sQuery(id+"F26.wireOp",EDGE,"E69")])]});
            var Q5;
            Q5=makeQuery(id+"F28.opPattern","COPY",BODY,{"derivedFrom":makeQuery(id+"F27.opExtrude","SWEPT_BODY",BODY,{"disambiguationData":[OSD([sQuery(id+"F26.wireOp",EDGE,"E66"),sQuery(id+"F26.wireOp",EDGE,"E67"),sQuery(id+"F26.wireOp",EDGE,"E68"),sQuery(id+"F26.wireOp",EDGE,"E69")])]}),"instanceName":"3"});
            var Q6;
            Q6=makeQuery(id+"F28.opPattern","COPY",BODY,{"derivedFrom":makeQuery(id+"F27.opExtrude","SWEPT_BODY",BODY,{"disambiguationData":[OSD([sQuery(id+"F26.wireOp",EDGE,"E66"),sQuery(id+"F26.wireOp",EDGE,"E67"),sQuery(id+"F26.wireOp",EDGE,"E68"),sQuery(id+"F26.wireOp",EDGE,"E69")])]}),"instanceName":"6"});
            var Q7;
            Q7=makeQuery(id+"F28.opPattern","COPY",BODY,{"derivedFrom":makeQuery(id+"F27.opExtrude","SWEPT_BODY",BODY,{"disambiguationData":[OSD([sQuery(id+"F26.wireOp",EDGE,"E66"),sQuery(id+"F26.wireOp",EDGE,"E67"),sQuery(id+"F26.wireOp",EDGE,"E68"),sQuery(id+"F26.wireOp",EDGE,"E69")])]}),"instanceName":"1"});
            var Q8;
            Q8=makeQuery(id+"F28.opPattern","COPY",BODY,{"derivedFrom":makeQuery(id+"F27.opExtrude","SWEPT_BODY",BODY,{"disambiguationData":[OSD([sQuery(id+"F26.wireOp",EDGE,"E66"),sQuery(id+"F26.wireOp",EDGE,"E67"),sQuery(id+"F26.wireOp",EDGE,"E68"),sQuery(id+"F26.wireOp",EDGE,"E69")])]}),"instanceName":"4"});
            var Q9;
            Q9=makeQuery(id+"F28.opPattern","COPY",BODY,{"derivedFrom":makeQuery(id+"F27.opExtrude","SWEPT_BODY",BODY,{"disambiguationData":[OSD([sQuery(id+"F26.wireOp",EDGE,"E66"),sQuery(id+"F26.wireOp",EDGE,"E67"),sQuery(id+"F26.wireOp",EDGE,"E68"),sQuery(id+"F26.wireOp",EDGE,"E69")])]}),"instanceName":"7"});
            var Q10;
            Q10=makeQuery(id+"F28.opPattern","COPY",BODY,{"derivedFrom":makeQuery(id+"F27.opExtrude","SWEPT_BODY",BODY,{"disambiguationData":[OSD([sQuery(id+"F26.wireOp",EDGE,"E66"),sQuery(id+"F26.wireOp",EDGE,"E67"),sQuery(id+"F26.wireOp",EDGE,"E68"),sQuery(id+"F26.wireOp",EDGE,"E69")])]}),"instanceName":"9"});
            var Q11;
            Q11=qCreatedBy(makeId("Right.planeOp"),FACE);
            mirror(context, id + "F29", {"entities" : qUnion([Q0, Q1, Q2, Q3, Q4, Q5, Q6, Q7, Q8, Q9, Q10]), "mirrorPlane" : qUnion([Q11])});
        }
        {
            var Q0;
            Q0=makeQuery(id+"F28.opPattern","COPY",BODY,{"derivedFrom":makeQuery(id+"F27.opExtrude","SWEPT_BODY",BODY,{"disambiguationData":[OSD([sQuery(id+"F26.wireOp",EDGE,"E66"),sQuery(id+"F26.wireOp",EDGE,"E67"),sQuery(id+"F26.wireOp",EDGE,"E68"),sQuery(id+"F26.wireOp",EDGE,"E69")])]}),"instanceName":"2"});
            var Q1;
            Q1=makeQuery(id+"F28.opPattern","COPY",BODY,{"derivedFrom":makeQuery(id+"F27.opExtrude","SWEPT_BODY",BODY,{"disambiguationData":[OSD([sQuery(id+"F26.wireOp",EDGE,"E66"),sQuery(id+"F26.wireOp",EDGE,"E67"),sQuery(id+"F26.wireOp",EDGE,"E68"),sQuery(id+"F26.wireOp",EDGE,"E69")])]}),"instanceName":"5"});
            var Q2;
            Q2=makeQuery(id+"F25.boolean.opBoolean","MERGE",BODY,{"derivedFrom":[makeQuery(id+"F9.opExtrude","SWEPT_BODY",BODY,{"disambiguationData":[OSD([sQuery(id+"F8.wireOp",EDGE,"E18.0"),sQuery(id+"F8.wireOp",EDGE,"E22.bottom"),sQuery(id+"F8.wireOp",EDGE,"E22.top"),sQuery(id+"F8.wireOp",EDGE,"E22.left"),sQuery(id+"F8.wireOp",EDGE,"E22.right")])]}),makeQuery(id+"F23.opExtrude","SWEPT_BODY",BODY,{"disambiguationData":[OSD([sQuery(id+"F22.wireOp",EDGE,"E57")])]}),makeQuery(id+"F25.opExtrude","SWEPT_BODY",BODY,{"disambiguationData":[OSD([sQuery(id+"F24.wireOp",EDGE,"E60"),sQuery(id+"F24.wireOp",EDGE,"E62"),sQuery(id+"F24.wireOp",EDGE,"E63"),sQuery(id+"F24.wireOp",EDGE,"E64")])]}),makeQuery(id+"F25.opExtrude","SWEPT_BODY",BODY,{"disambiguationData":[OSD([sQuery(id+"F24.wireOp",EDGE,"E65.1.0"),sQuery(id+"F24.wireOp",EDGE,"E65.1.1"),sQuery(id+"F24.wireOp",EDGE,"E65.1.2"),sQuery(id+"F24.wireOp",EDGE,"E65.1.4")])]}),makeQuery(id+"F25.opExtrude","SWEPT_BODY",BODY,{"disambiguationData":[OSD([sQuery(id+"F24.wireOp",EDGE,"E65.2.0"),sQuery(id+"F24.wireOp",EDGE,"E65.2.1"),sQuery(id+"F24.wireOp",EDGE,"E65.2.2"),sQuery(id+"F24.wireOp",EDGE,"E65.2.4")])]}),makeQuery(id+"F25.opExtrude","SWEPT_BODY",BODY,{"disambiguationData":[OSD([sQuery(id+"F24.wireOp",EDGE,"E65.3.0"),sQuery(id+"F24.wireOp",EDGE,"E65.3.1"),sQuery(id+"F24.wireOp",EDGE,"E65.3.2"),sQuery(id+"F24.wireOp",EDGE,"E65.3.4")])]})]});
            var Q3;
            Q3=makeQuery(id+"F28.opPattern","COPY",BODY,{"derivedFrom":makeQuery(id+"F27.opExtrude","SWEPT_BODY",BODY,{"disambiguationData":[OSD([sQuery(id+"F26.wireOp",EDGE,"E66"),sQuery(id+"F26.wireOp",EDGE,"E67"),sQuery(id+"F26.wireOp",EDGE,"E68"),sQuery(id+"F26.wireOp",EDGE,"E69")])]}),"instanceName":"8"});
            var Q4;
            Q4=makeQuery(id+"F27.opExtrude","SWEPT_BODY",BODY,{"disambiguationData":[OSD([sQuery(id+"F26.wireOp",EDGE,"E66"),sQuery(id+"F26.wireOp",EDGE,"E67"),sQuery(id+"F26.wireOp",EDGE,"E68"),sQuery(id+"F26.wireOp",EDGE,"E69")])]});
            var Q5;
            Q5=makeQuery(id+"F28.opPattern","COPY",BODY,{"derivedFrom":makeQuery(id+"F27.opExtrude","SWEPT_BODY",BODY,{"disambiguationData":[OSD([sQuery(id+"F26.wireOp",EDGE,"E66"),sQuery(id+"F26.wireOp",EDGE,"E67"),sQuery(id+"F26.wireOp",EDGE,"E68"),sQuery(id+"F26.wireOp",EDGE,"E69")])]}),"instanceName":"3"});
            var Q6;
            Q6=makeQuery(id+"F28.opPattern","COPY",BODY,{"derivedFrom":makeQuery(id+"F27.opExtrude","SWEPT_BODY",BODY,{"disambiguationData":[OSD([sQuery(id+"F26.wireOp",EDGE,"E66"),sQuery(id+"F26.wireOp",EDGE,"E67"),sQuery(id+"F26.wireOp",EDGE,"E68"),sQuery(id+"F26.wireOp",EDGE,"E69")])]}),"instanceName":"6"});
            var Q7;
            Q7=makeQuery(id+"F28.opPattern","COPY",BODY,{"derivedFrom":makeQuery(id+"F27.opExtrude","SWEPT_BODY",BODY,{"disambiguationData":[OSD([sQuery(id+"F26.wireOp",EDGE,"E66"),sQuery(id+"F26.wireOp",EDGE,"E67"),sQuery(id+"F26.wireOp",EDGE,"E68"),sQuery(id+"F26.wireOp",EDGE,"E69")])]}),"instanceName":"1"});
            var Q8;
            Q8=makeQuery(id+"F28.opPattern","COPY",BODY,{"derivedFrom":makeQuery(id+"F27.opExtrude","SWEPT_BODY",BODY,{"disambiguationData":[OSD([sQuery(id+"F26.wireOp",EDGE,"E66"),sQuery(id+"F26.wireOp",EDGE,"E67"),sQuery(id+"F26.wireOp",EDGE,"E68"),sQuery(id+"F26.wireOp",EDGE,"E69")])]}),"instanceName":"4"});
            var Q9;
            Q9=makeQuery(id+"F28.opPattern","COPY",BODY,{"derivedFrom":makeQuery(id+"F27.opExtrude","SWEPT_BODY",BODY,{"disambiguationData":[OSD([sQuery(id+"F26.wireOp",EDGE,"E66"),sQuery(id+"F26.wireOp",EDGE,"E67"),sQuery(id+"F26.wireOp",EDGE,"E68"),sQuery(id+"F26.wireOp",EDGE,"E69")])]}),"instanceName":"7"});
            var Q10;
            Q10=makeQuery(id+"F28.opPattern","COPY",BODY,{"derivedFrom":makeQuery(id+"F27.opExtrude","SWEPT_BODY",BODY,{"disambiguationData":[OSD([sQuery(id+"F26.wireOp",EDGE,"E66"),sQuery(id+"F26.wireOp",EDGE,"E67"),sQuery(id+"F26.wireOp",EDGE,"E68"),sQuery(id+"F26.wireOp",EDGE,"E69")])]}),"instanceName":"9"});
            var Q11;
            Q11=makeQuery(id+"F29.opPattern","COPY",BODY,{"derivedFrom":makeQuery(id+"F28.opPattern","COPY",BODY,{"derivedFrom":makeQuery(id+"F27.opExtrude","SWEPT_BODY",BODY,{"disambiguationData":[OSD([sQuery(id+"F26.wireOp",EDGE,"E66"),sQuery(id+"F26.wireOp",EDGE,"E67"),sQuery(id+"F26.wireOp",EDGE,"E68"),sQuery(id+"F26.wireOp",EDGE,"E69")])]}),"instanceName":"1"}),"instanceName":"1"});
            var Q12;
            Q12=makeQuery(id+"F29.opPattern","COPY",BODY,{"derivedFrom":makeQuery(id+"F27.opExtrude","SWEPT_BODY",BODY,{"disambiguationData":[OSD([sQuery(id+"F26.wireOp",EDGE,"E66"),sQuery(id+"F26.wireOp",EDGE,"E67"),sQuery(id+"F26.wireOp",EDGE,"E68"),sQuery(id+"F26.wireOp",EDGE,"E69")])]}),"instanceName":"1"});
            var Q13;
            Q13=makeQuery(id+"F29.opPattern","COPY",BODY,{"derivedFrom":makeQuery(id+"F25.boolean.opBoolean","MERGE",BODY,{"derivedFrom":[makeQuery(id+"F9.opExtrude","SWEPT_BODY",BODY,{"disambiguationData":[OSD([sQuery(id+"F8.wireOp",EDGE,"E18.0"),sQuery(id+"F8.wireOp",EDGE,"E22.bottom"),sQuery(id+"F8.wireOp",EDGE,"E22.top"),sQuery(id+"F8.wireOp",EDGE,"E22.left"),sQuery(id+"F8.wireOp",EDGE,"E22.right")])]}),makeQuery(id+"F23.opExtrude","SWEPT_BODY",BODY,{"disambiguationData":[OSD([sQuery(id+"F22.wireOp",EDGE,"E57")])]}),makeQuery(id+"F25.opExtrude","SWEPT_BODY",BODY,{"disambiguationData":[OSD([sQuery(id+"F24.wireOp",EDGE,"E60"),sQuery(id+"F24.wireOp",EDGE,"E62"),sQuery(id+"F24.wireOp",EDGE,"E63"),sQuery(id+"F24.wireOp",EDGE,"E64")])]}),makeQuery(id+"F25.opExtrude","SWEPT_BODY",BODY,{"disambiguationData":[OSD([sQuery(id+"F24.wireOp",EDGE,"E65.1.0"),sQuery(id+"F24.wireOp",EDGE,"E65.1.1"),sQuery(id+"F24.wireOp",EDGE,"E65.1.2"),sQuery(id+"F24.wireOp",EDGE,"E65.1.4")])]}),makeQuery(id+"F25.opExtrude","SWEPT_BODY",BODY,{"disambiguationData":[OSD([sQuery(id+"F24.wireOp",EDGE,"E65.2.0"),sQuery(id+"F24.wireOp",EDGE,"E65.2.1"),sQuery(id+"F24.wireOp",EDGE,"E65.2.2"),sQuery(id+"F24.wireOp",EDGE,"E65.2.4")])]}),makeQuery(id+"F25.opExtrude","SWEPT_BODY",BODY,{"disambiguationData":[OSD([sQuery(id+"F24.wireOp",EDGE,"E65.3.0"),sQuery(id+"F24.wireOp",EDGE,"E65.3.1"),sQuery(id+"F24.wireOp",EDGE,"E65.3.2"),sQuery(id+"F24.wireOp",EDGE,"E65.3.4")])]})]}),"instanceName":"1"});
            var Q14;
            Q14=makeQuery(id+"F29.opPattern","COPY",BODY,{"derivedFrom":makeQuery(id+"F28.opPattern","COPY",BODY,{"derivedFrom":makeQuery(id+"F27.opExtrude","SWEPT_BODY",BODY,{"disambiguationData":[OSD([sQuery(id+"F26.wireOp",EDGE,"E66"),sQuery(id+"F26.wireOp",EDGE,"E67"),sQuery(id+"F26.wireOp",EDGE,"E68"),sQuery(id+"F26.wireOp",EDGE,"E69")])]}),"instanceName":"4"}),"instanceName":"1"});
            var Q15;
            Q15=makeQuery(id+"F29.opPattern","COPY",BODY,{"derivedFrom":makeQuery(id+"F28.opPattern","COPY",BODY,{"derivedFrom":makeQuery(id+"F27.opExtrude","SWEPT_BODY",BODY,{"disambiguationData":[OSD([sQuery(id+"F26.wireOp",EDGE,"E66"),sQuery(id+"F26.wireOp",EDGE,"E67"),sQuery(id+"F26.wireOp",EDGE,"E68"),sQuery(id+"F26.wireOp",EDGE,"E69")])]}),"instanceName":"5"}),"instanceName":"1"});
            var Q16;
            Q16=makeQuery(id+"F29.opPattern","COPY",BODY,{"derivedFrom":makeQuery(id+"F28.opPattern","COPY",BODY,{"derivedFrom":makeQuery(id+"F27.opExtrude","SWEPT_BODY",BODY,{"disambiguationData":[OSD([sQuery(id+"F26.wireOp",EDGE,"E66"),sQuery(id+"F26.wireOp",EDGE,"E67"),sQuery(id+"F26.wireOp",EDGE,"E68"),sQuery(id+"F26.wireOp",EDGE,"E69")])]}),"instanceName":"3"}),"instanceName":"1"});
            var Q17;
            Q17=makeQuery(id+"F29.opPattern","COPY",BODY,{"derivedFrom":makeQuery(id+"F28.opPattern","COPY",BODY,{"derivedFrom":makeQuery(id+"F27.opExtrude","SWEPT_BODY",BODY,{"disambiguationData":[OSD([sQuery(id+"F26.wireOp",EDGE,"E66"),sQuery(id+"F26.wireOp",EDGE,"E67"),sQuery(id+"F26.wireOp",EDGE,"E68"),sQuery(id+"F26.wireOp",EDGE,"E69")])]}),"instanceName":"8"}),"instanceName":"1"});
            var Q18;
            Q18=makeQuery(id+"F29.opPattern","COPY",BODY,{"derivedFrom":makeQuery(id+"F28.opPattern","COPY",BODY,{"derivedFrom":makeQuery(id+"F27.opExtrude","SWEPT_BODY",BODY,{"disambiguationData":[OSD([sQuery(id+"F26.wireOp",EDGE,"E66"),sQuery(id+"F26.wireOp",EDGE,"E67"),sQuery(id+"F26.wireOp",EDGE,"E68"),sQuery(id+"F26.wireOp",EDGE,"E69")])]}),"instanceName":"6"}),"instanceName":"1"});
            var Q19;
            Q19=makeQuery(id+"F29.opPattern","COPY",BODY,{"derivedFrom":makeQuery(id+"F28.opPattern","COPY",BODY,{"derivedFrom":makeQuery(id+"F27.opExtrude","SWEPT_BODY",BODY,{"disambiguationData":[OSD([sQuery(id+"F26.wireOp",EDGE,"E66"),sQuery(id+"F26.wireOp",EDGE,"E67"),sQuery(id+"F26.wireOp",EDGE,"E68"),sQuery(id+"F26.wireOp",EDGE,"E69")])]}),"instanceName":"7"}),"instanceName":"1"});
            var Q20;
            Q20=makeQuery(id+"F29.opPattern","COPY",BODY,{"derivedFrom":makeQuery(id+"F28.opPattern","COPY",BODY,{"derivedFrom":makeQuery(id+"F27.opExtrude","SWEPT_BODY",BODY,{"disambiguationData":[OSD([sQuery(id+"F26.wireOp",EDGE,"E66"),sQuery(id+"F26.wireOp",EDGE,"E67"),sQuery(id+"F26.wireOp",EDGE,"E68"),sQuery(id+"F26.wireOp",EDGE,"E69")])]}),"instanceName":"2"}),"instanceName":"1"});
            var Q21;
            Q21=makeQuery(id+"F29.opPattern","COPY",BODY,{"derivedFrom":makeQuery(id+"F28.opPattern","COPY",BODY,{"derivedFrom":makeQuery(id+"F27.opExtrude","SWEPT_BODY",BODY,{"disambiguationData":[OSD([sQuery(id+"F26.wireOp",EDGE,"E66"),sQuery(id+"F26.wireOp",EDGE,"E67"),sQuery(id+"F26.wireOp",EDGE,"E68"),sQuery(id+"F26.wireOp",EDGE,"E69")])]}),"instanceName":"9"}),"instanceName":"1"});
            var Q22;
            Q22=qCreatedBy(makeId("Top.planeOp"),FACE);
            mirror(context, id + "F30", {"entities" : qUnion([Q0, Q1, Q2, Q3, Q4, Q5, Q6, Q7, Q8, Q9, Q10, Q11, Q12, Q13, Q14, Q15, Q16, Q17, Q18, Q19, Q20, Q21]), "mirrorPlane" : qUnion([Q22])});
        }
        {
            var Q0;
            Q0=makeQuery(id+"F17.opExtrude","CAP_FACE",FACE,{"disambiguationData":[OSD([sQuery(id+"F16.wireOp",EDGE,"E52.bottom"),sQuery(id+"F16.wireOp",EDGE,"E52.top"),sQuery(id+"F16.wireOp",EDGE,"E52.left"),sQuery(id+"F16.wireOp",EDGE,"E52.right")])],"isStart":false});
            var sketch = newSketch(context, id + "F31", { "sketchPlane" : qUnion([Q0])});
            skLineSegment(sketch, "E77.bottom", {"start": v(5, -144.3) * mm, "end": v(-5, -144.3) * mm});
            skLineSegment(sketch, "E77.top", {"start": v(5, 144.3) * mm, "end": v(-5, 144.3) * mm});
            skLineSegment(sketch, "E77.left", {"start": v(5, -144.3) * mm, "end": v(5, 144.3) * mm});
            skLineSegment(sketch, "E77.right", {"start": v(-5, -144.3) * mm, "end": v(-5, 144.3) * mm});
            skPoint(sketch, "E77.middle", {"position": v(0, 0) * mm});
            skLineSegment(sketch, "E78.bottom", {"start": v(-30, -144.3) * mm, "end": v(-40, -144.3) * mm});
            skLineSegment(sketch, "E78.top", {"start": v(-30, 144.3) * mm, "end": v(-40, 144.3) * mm});
            skLineSegment(sketch, "E78.left", {"start": v(-30, -144.3) * mm, "end": v(-30, 144.3) * mm});
            skLineSegment(sketch, "E78.right", {"start": v(-40, -144.3) * mm, "end": v(-40, 144.3) * mm});
            skPoint(sketch, "E78.middle", {"position": v(-35, 0) * mm});
            skLineSegment(sketch, "E79.bottom", {"start": v(-65, -144.3) * mm, "end": v(-75, -144.3) * mm});
            skLineSegment(sketch, "E79.top", {"start": v(-65, 144.3) * mm, "end": v(-75, 144.3) * mm});
            skLineSegment(sketch, "E79.left", {"start": v(-65, -144.3) * mm, "end": v(-65, 144.3) * mm});
            skLineSegment(sketch, "E79.right", {"start": v(-75, -144.3) * mm, "end": v(-75, 144.3) * mm});
            skPoint(sketch, "E79.middle", {"position": v(-70, 0) * mm});
            skLineSegment(sketch, "E80.bottom", {"start": v(-100, -144.3) * mm, "end": v(-110, -144.3) * mm});
            skLineSegment(sketch, "E80.top", {"start": v(-100, 144.3) * mm, "end": v(-110, 144.3) * mm});
            skLineSegment(sketch, "E80.left", {"start": v(-100, -144.3) * mm, "end": v(-100, 144.3) * mm});
            skLineSegment(sketch, "E80.right", {"start": v(-110, -144.3) * mm, "end": v(-110, 144.3) * mm});
            skPoint(sketch, "E80.middle", {"position": v(-105, 0) * mm});
            skLineSegment(sketch, "E81.bottom", {"start": v(-145, -144.3) * mm, "end": v(-135, -144.3) * mm});
            skLineSegment(sketch, "E81.top", {"start": v(-145, 144.3) * mm, "end": v(-135, 144.3) * mm});
            skLineSegment(sketch, "E81.left", {"start": v(-145, -144.3) * mm, "end": v(-145, 144.3) * mm});
            skLineSegment(sketch, "E81.right", {"start": v(-135, -144.3) * mm, "end": v(-135, 144.3) * mm});
            skPoint(sketch, "E81.middle", {"position": v(-140, 0) * mm});
            skLineSegment(sketch, "E82.bottom", {"start": v(-170, -144.3) * mm, "end": v(-180, -144.3) * mm});
            skLineSegment(sketch, "E82.top", {"start": v(-170, 144.3) * mm, "end": v(-180, 144.3) * mm});
            skLineSegment(sketch, "E82.left", {"start": v(-170, -144.3) * mm, "end": v(-170, 144.3) * mm});
            skLineSegment(sketch, "E82.right", {"start": v(-180, -144.3) * mm, "end": v(-180, 144.3) * mm});
            skPoint(sketch, "E82.middle", {"position": v(-175, 0) * mm});
            skLineSegment(sketch, "E83.bottom", {"start": v(30, -144.3) * mm, "end": v(40, -144.3) * mm});
            skLineSegment(sketch, "E83.top", {"start": v(30, 144.3) * mm, "end": v(40, 144.3) * mm});
            skLineSegment(sketch, "E83.left", {"start": v(30, -144.3) * mm, "end": v(30, 144.3) * mm});
            skLineSegment(sketch, "E83.right", {"start": v(40, -144.3) * mm, "end": v(40, 144.3) * mm});
            skPoint(sketch, "E83.middle", {"position": v(35, 0) * mm});
            skLineSegment(sketch, "E84.bottom", {"start": v(75, -144.3) * mm, "end": v(65, -144.3) * mm});
            skLineSegment(sketch, "E84.top", {"start": v(75, 144.3) * mm, "end": v(65, 144.3) * mm});
            skLineSegment(sketch, "E84.left", {"start": v(75, -144.3) * mm, "end": v(75, 144.3) * mm});
            skLineSegment(sketch, "E84.right", {"start": v(65, -144.3) * mm, "end": v(65, 144.3) * mm});
            skPoint(sketch, "E84.middle", {"position": v(70, 0) * mm});
            skLineSegment(sketch, "E85.bottom", {"start": v(110, -144.3) * mm, "end": v(100, -144.3) * mm});
            skLineSegment(sketch, "E85.top", {"start": v(110, 144.3) * mm, "end": v(100, 144.3) * mm});
            skLineSegment(sketch, "E85.left", {"start": v(110, -144.3) * mm, "end": v(110, 144.3) * mm});
            skLineSegment(sketch, "E85.right", {"start": v(100, -144.3) * mm, "end": v(100, 144.3) * mm});
            skPoint(sketch, "E85.middle", {"position": v(105, 0) * mm});
            skLineSegment(sketch, "E86.bottom", {"start": v(145, -144.3) * mm, "end": v(135, -144.3) * mm});
            skLineSegment(sketch, "E86.top", {"start": v(145, 144.3) * mm, "end": v(135, 144.3) * mm});
            skLineSegment(sketch, "E86.left", {"start": v(145, -144.3) * mm, "end": v(145, 144.3) * mm});
            skLineSegment(sketch, "E86.right", {"start": v(135, -144.3) * mm, "end": v(135, 144.3) * mm});
            skPoint(sketch, "E86.middle", {"position": v(140, 0) * mm});
            skLineSegment(sketch, "E87.bottom", {"start": v(180, -144.3) * mm, "end": v(170, -144.3) * mm});
            skLineSegment(sketch, "E87.top", {"start": v(180, 144.3) * mm, "end": v(170, 144.3) * mm});
            skLineSegment(sketch, "E87.left", {"start": v(180, -144.3) * mm, "end": v(180, 144.3) * mm});
            skLineSegment(sketch, "E87.right", {"start": v(170, -144.3) * mm, "end": v(170, 144.3) * mm});
            skPoint(sketch, "E87.middle", {"position": v(175, 0) * mm});
            skLineSegment(sketch, "E88", {"start": v(0, 0) * mm, "end": v(0, -130.97) * mm, "construction": true});
            skSolve(sketch);
        }
        {
            var Q0;
            Q0 = qSketchRegion(id + "F31", true);
            extrude(context, id + "F32", {"entities" : qUnion([Q0]), "depth" : 3 * mm});
        }
    });
